# Revit family: EBB
name_source: partatom
category: Lighting Fixtures
revit_build: Autodesk Revit 2014 (Build: 20130308_1515(x64)
units: mm (PartAtom-declared; Revit-internal decimal feet)

## types (1)
- EBB
    Apparent Load = 20 VA
    Application = Certified to UL924 Standards
UL 844 Hazardous Location Listed
    Certification = UL 924 Listed
NFPA 101 Life Safety Code
CEC T20 Compliant
    Color Filter = 16777215
    Default Elevation = 48.000"
    Description = Self-contained hazardous location emergency light which provides 90 minutes of emergency illumination in environments with high concentrations of gas, explosive vapors and dust
    Dimming Lamp Color Temperature Shift = <None>
    Emit Shape Visible in Rendering = No
    Emit from Circle Diameter = 24.000"
    Features = Emergency luminaire in explosion proof applications
• Medium-Gray, epoxy-clad, copper-free aluminum housing
• Impact resistant, prismatic glass globes with incandescent lamps
• Temperature range: 0ºC to 40ºC (32ºF to 104ºF)
• UL 924 and 844 listed for NEC C1D1 & C1D2 Groups C & D, C2D1 & C2D2, C3D1 & C3D2
    Finish = Hubbell - White
    Glass = Hubbell - light Glass
    Holder Material = Hubbell - Steel
    Lamp = LED Lamp
    Lens = Hubbell - Red Glass
    Load Classification = Lighting
    Manufacturer = DUAL-LITE
    Model = EBB
    Photometric Web File = generic
    Product Documentation Link = https://hubbellcdn.com
    Product Page URL = https://www.hubbell.com
    Tilt Angle = 60.00°
    Type Comments = Exit Light
    URL = https://www.hubbell.com
    Wall Plate Material = Hubbell - Black
    Warranty = Fixture: 5 Years Full; Battery: 2 Years Full, 8 Years Pro-Rata
    Wattage Comments = 20W
    Watts = 20 W

## geometry (parser evidence)
native form markers: Blend x8, Sweep x2
no freeform markers — native parametric forms only
